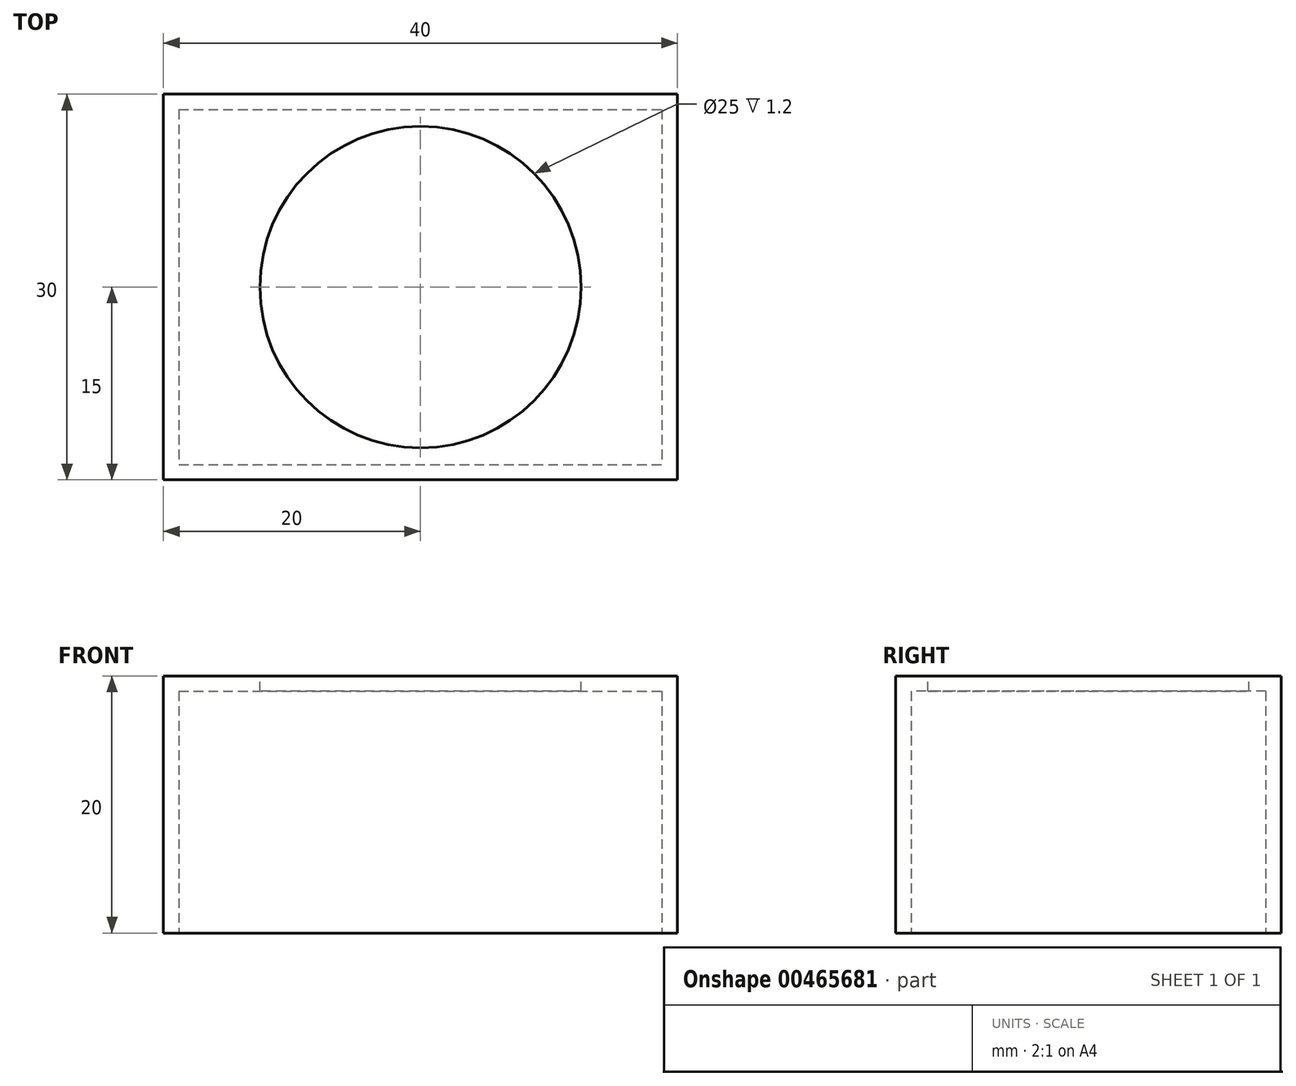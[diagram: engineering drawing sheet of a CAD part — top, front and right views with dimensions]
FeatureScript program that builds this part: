
annotation { "Feature Type Name" : "Feature", "Feature Type Description" : "" }
export const myFeature = defineFeature(function(context is Context, id is Id, definition is map)
    precondition{}
    {
        {
            var Q0;
            Q0=qCreatedBy(makeId("Top.planeOp"),FACE);
            var sketch = newSketch(context, id + "F0", { "sketchPlane" : qUnion([Q0])});
            skLineSegment(sketch, "E0.bottom", {"start": v(0, 0) * mm, "end": v(40, 0) * mm});
            skLineSegment(sketch, "E0.top", {"start": v(0, -30) * mm, "end": v(40, -30) * mm});
            skLineSegment(sketch, "E0.left", {"start": v(0, 0) * mm, "end": v(0, -30) * mm});
            skLineSegment(sketch, "E0.right", {"start": v(40, 0) * mm, "end": v(40, -30) * mm});
            skSolve(sketch);
        }
        {
            var Q0;
            Q0=makeQuery(id+"F0.imprint","IMPRINT",FACE,{"disambiguationData":[TD([[makeQuery(id+"F0.imprint","IMPRINT",EDGE,{"derivedFrom":sQuery(id+"F0.wireOp",EDGE,"E0.bottom")}),-1.0]])]});
            extrude(context, id + "F1", {"entities" : qUnion([Q0]), "depth" : 20 * mm});
        }
        {
            var Q0;
            Q0=makeQuery(id+"F1.opExtrude","CAP_FACE",FACE,{"disambiguationData":[OSD([sQuery(id+"F0.wireOp",EDGE,"E0.bottom"),sQuery(id+"F0.wireOp",EDGE,"E0.top"),sQuery(id+"F0.wireOp",EDGE,"E0.left"),sQuery(id+"F0.wireOp",EDGE,"E0.right")])],"isStart":true});
            shell(context, id + "F2", {"entities" : qUnion([Q0]), "thickness" : 1.2 * mm});
        }
        {
            var Q0;
            Q0=makeQuery(id+"F1.opExtrude","CAP_FACE",FACE,{"disambiguationData":[OSD([sQuery(id+"F0.wireOp",EDGE,"E0.bottom"),sQuery(id+"F0.wireOp",EDGE,"E0.top"),sQuery(id+"F0.wireOp",EDGE,"E0.left"),sQuery(id+"F0.wireOp",EDGE,"E0.right")])],"isStart":false});
            var sketch = newSketch(context, id + "F3", { "sketchPlane" : qUnion([Q0])});
            skCircle(sketch, "E1", {"center": v(20, -15) * mm, "radius": 12.5 * mm});
            skSolve(sketch);
        }
        {
            var Q0;
            Q0=sQuery(id+"F3.wireOp",VERTEX,"E1.center");
            var Q1;
            Q1=makeQuery(id+"F1.opExtrude","SWEPT_BODY",BODY,{"disambiguationData":[OSD([sQuery(id+"F0.wireOp",EDGE,"E0.bottom"),sQuery(id+"F0.wireOp",EDGE,"E0.top"),sQuery(id+"F0.wireOp",EDGE,"E0.left"),sQuery(id+"F0.wireOp",EDGE,"E0.right")])]});
            hole(context, id + "F4", {"style" : HoleStyle.SIMPLE, "endStyle" : HoleEndStyle.THROUGH, "holeDiameter" : 25 * mm, "isTappedThrough" : true, "tappedDepth" : 12 * mm, "tapClearance" : 3, "locations" : qUnion([Q0]), "scope" : qUnion([Q1])});
        }
    });
